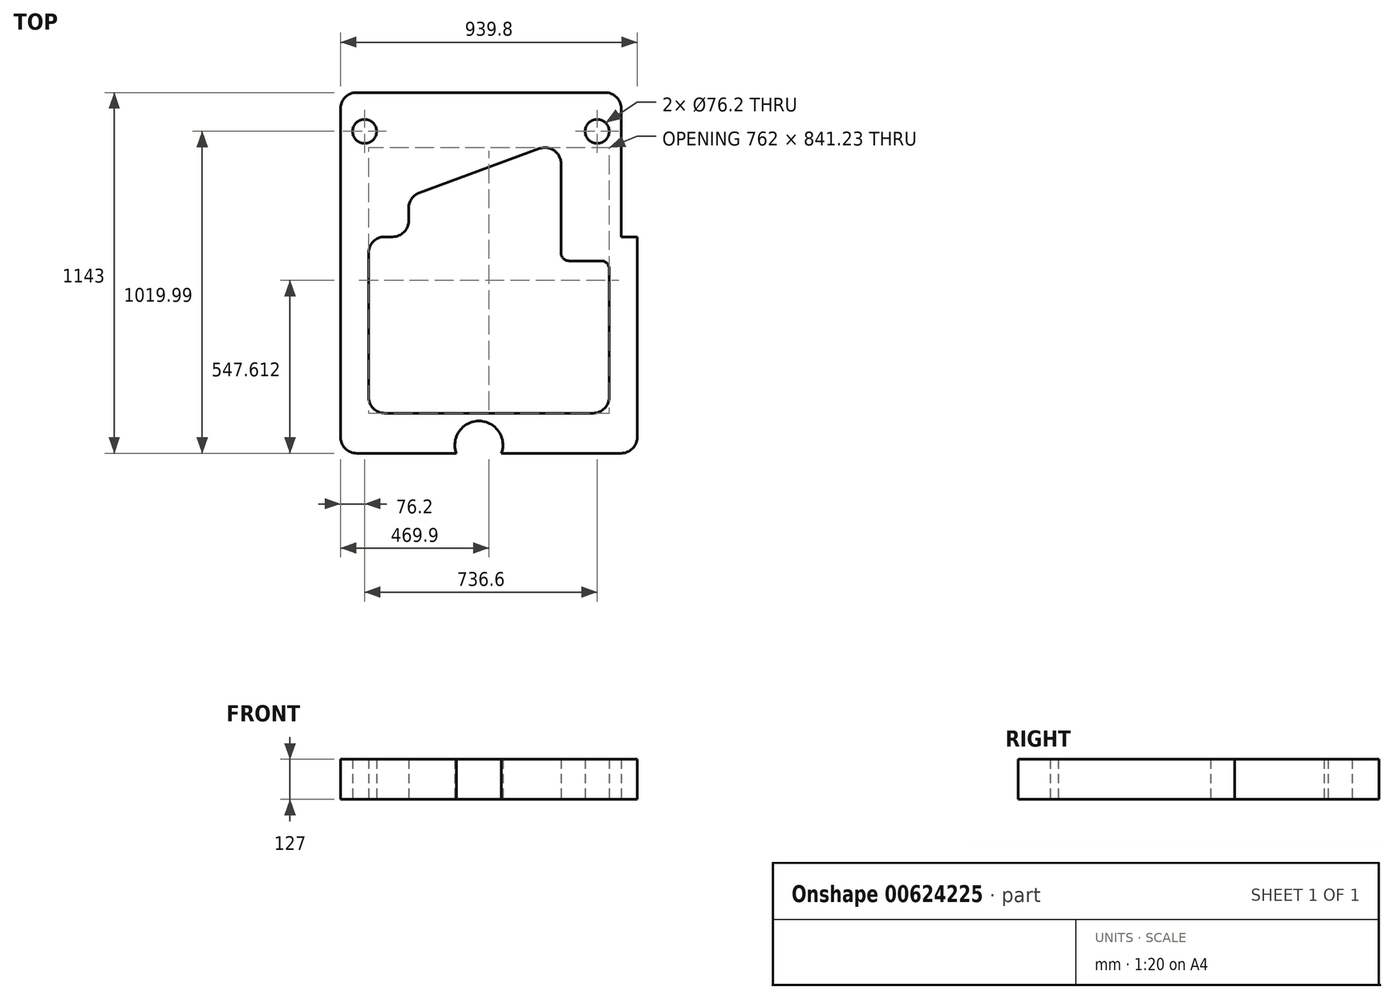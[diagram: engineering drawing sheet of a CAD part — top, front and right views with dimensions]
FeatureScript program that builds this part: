
annotation { "Feature Type Name" : "Feature", "Feature Type Description" : "" }
export const myFeature = defineFeature(function(context is Context, id is Id, definition is map)
    precondition{}
    {
        {
            var Q0;
            Q0=qCreatedBy(makeId("Top.planeOp"),FACE);
            var sketch = newSketch(context, id + "F0", { "sketchPlane" : qUnion([Q0])});
            skLineSegment(sketch, "E0.bottom", {"start": v(368.3, 571.5) * mm, "end": v(-419.1, 571.5) * mm});
            skLineSegment(sketch, "E0.top", {"start": v(419.1, -571.5) * mm, "end": v(-419.1, -571.5) * mm});
            skLineSegment(sketch, "E0.left", {"start": v(469.9, 114.3) * mm, "end": v(469.9, -520.7) * mm});
            skLineSegment(sketch, "E0.right", {"start": v(-469.9, 520.7) * mm, "end": v(-469.9, -520.7) * mm});
            skPoint(sketch, "E0.middle", {"position": v(0, 0) * mm});
            skLineSegment(sketch, "E1", {"start": v(-381, 63.5) * mm, "end": v(-381, -393.7) * mm});
            skLineSegment(sketch, "E2", {"start": v(-330.2, -444.5) * mm, "end": v(330.2, -444.5) * mm});
            skLineSegment(sketch, "E3", {"start": v(381, -393.7) * mm, "end": v(381, 12.7) * mm});
            skLineSegment(sketch, "E4", {"start": v(-330.2, 114.3) * mm, "end": v(-304.8, 114.3) * mm});
            skLineSegment(sketch, "E5", {"start": v(-254, 165.1) * mm, "end": v(-254, 205.88) * mm});
            skLineSegment(sketch, "E6", {"start": v(-220.76, 253.55) * mm, "end": v(160.24, 393.91) * mm});
            skLineSegment(sketch, "E7", {"start": v(228.6, 346.25) * mm, "end": v(228.6, 63.5) * mm});
            skLineSegment(sketch, "E8", {"start": v(254, 38.1) * mm, "end": v(355.6, 38.1) * mm});
            skLineSegment(sketch, "E9", {"start": v(419.1, 520.7) * mm, "end": v(419.1, 114.3) * mm});
            skLineSegment(sketch, "E10", {"start": v(419.1, 114.3) * mm, "end": v(508, 114.3) * mm});
            skPoint(sketch, "E11.orphan", {"position": v(469.9, 571.5) * mm});
            skPoint(sketch, "E12.visualSharp", {"position": v(-254, 114.3) * mm});
            skArc(sketch, "E12.filletArc", {"start": v(-304.8, 114.3) * mm, "mid": v(-268.88, 129.18) * mm, "end": v(-254, 165.1) * mm});
            skPoint(sketch, "E13.visualSharp", {"position": v(-381, 114.3) * mm});
            skArc(sketch, "E13.filletArc", {"start": v(-330.2, 114.3) * mm, "mid": v(-366.12, 99.42) * mm, "end": v(-381, 63.5) * mm});
            skPoint(sketch, "E14.visualSharp", {"position": v(-381, -444.5) * mm});
            skArc(sketch, "E14.filletArc", {"start": v(-381, -393.7) * mm, "mid": v(-366.12, -429.62) * mm, "end": v(-330.2, -444.5) * mm});
            skPoint(sketch, "E15.visualSharp", {"position": v(381, -444.5) * mm});
            skArc(sketch, "E15.filletArc", {"start": v(330.2, -444.5) * mm, "mid": v(366.12, -429.62) * mm, "end": v(381, -393.7) * mm});
            skPoint(sketch, "E16.visualSharp", {"position": v(-254, 241.3) * mm});
            skArc(sketch, "E16.filletArc", {"start": v(-220.76, 253.55) * mm, "mid": v(-244.87, 234.93) * mm, "end": v(-254, 205.88) * mm});
            skPoint(sketch, "E17.visualSharp", {"position": v(228.6, 419.1) * mm});
            skArc(sketch, "E17.filletArc", {"start": v(228.6, 346.25) * mm, "mid": v(206.86, 387.92) * mm, "end": v(160.24, 393.91) * mm});
            skPoint(sketch, "E18.visualSharp", {"position": v(228.6, 38.1) * mm});
            skArc(sketch, "E18.filletArc", {"start": v(228.6, 63.5) * mm, "mid": v(236.04, 45.54) * mm, "end": v(254, 38.1) * mm});
            skPoint(sketch, "E19.visualSharp", {"position": v(381, 38.1) * mm});
            skArc(sketch, "E19.filletArc", {"start": v(381, 12.7) * mm, "mid": v(373.56, 30.66) * mm, "end": v(355.6, 38.1) * mm});
            skPoint(sketch, "E20.visualSharp", {"position": v(-469.9, 571.5) * mm});
            skArc(sketch, "E20.filletArc", {"start": v(-419.1, 571.5) * mm, "mid": v(-455.02, 556.62) * mm, "end": v(-469.9, 520.7) * mm});
            skPoint(sketch, "E21.visualSharp", {"position": v(-469.9, -571.5) * mm});
            skArc(sketch, "E21.filletArc", {"start": v(-469.9, -520.7) * mm, "mid": v(-455.02, -556.62) * mm, "end": v(-419.1, -571.5) * mm});
            skPoint(sketch, "E22.visualSharp", {"position": v(469.9, -571.5) * mm});
            skArc(sketch, "E22.filletArc", {"start": v(419.1, -571.5) * mm, "mid": v(455.02, -556.62) * mm, "end": v(469.9, -520.7) * mm});
            skArc(sketch, "E23.filletArc", {"start": v(419.1, 520.7) * mm, "mid": v(404.22, 556.62) * mm, "end": v(368.3, 571.5) * mm});
            skLineSegment(sketch, "E24", {"start": v(-355.6, -508) * mm, "end": v(355.6, -508) * mm});
            skLineSegment(sketch, "E25", {"start": v(-381, -393.7) * mm, "end": v(-381, -482.6) * mm});
            skLineSegment(sketch, "E26", {"start": v(381, -393.7) * mm, "end": v(381, -482.6) * mm});
            skPoint(sketch, "E27.visualSharp", {"position": v(-381, -508) * mm});
            skArc(sketch, "E27.filletArc", {"start": v(-381, -482.6) * mm, "mid": v(-373.56, -500.56) * mm, "end": v(-355.6, -508) * mm});
            skPoint(sketch, "E28.visualSharp", {"position": v(381, -508) * mm});
            skArc(sketch, "E28.filletArc", {"start": v(355.6, -508) * mm, "mid": v(373.56, -500.56) * mm, "end": v(381, -482.6) * mm});
            skLineSegment(sketch, "E29", {"start": v(-31.69, -444.5) * mm, "end": v(-31.69, -624.57) * mm, "construction": true});
            skCircle(sketch, "E30", {"center": v(-31.69, -545.67) * mm, "radius": 76.2 * mm});
            skCircle(sketch, "E31", {"center": v(-31.69, -545.67) * mm, "radius": 38.1 * mm});
            skCircle(sketch, "E32", {"center": v(-393.7, 448.5) * mm, "radius": 76.2 * mm});
            skCircle(sketch, "E33", {"center": v(-393.7, 448.5) * mm, "radius": 38.1 * mm});
            skLineSegment(sketch, "E34", {"start": v(-393.7, 448.5) * mm, "end": v(350.76, 448.5) * mm, "construction": true});
            skCircle(sketch, "E35", {"center": v(342.9, 448.5) * mm, "radius": 76.2 * mm});
            skCircle(sketch, "E36", {"center": v(342.9, 448.5) * mm, "radius": 38.1 * mm});
            skSolve(sketch);
        }
        {
            var Q0;
            Q0=makeQuery(id+"F0.imprint","IMPRINT",FACE,{"disambiguationData":[TD([[makeQuery(id+"F0.imprint","IMPRINT",EDGE,{"derivedFrom":sQuery(id+"F0.wireOp",EDGE,"E2")}),-1.0]])]});
            extrude(context, id + "F1", {"entities" : qUnion([Q0]), "depth" : 50.8 * mm, "offsetDistance" : 25.4 * mm});
        }
        {
            var Q0;
            Q0=makeQuery(id+"F0.imprint","IMPRINT",FACE,{"disambiguationData":[TD([[makeQuery(id+"F0.imprint","IMPRINT",EDGE,{"derivedFrom":sQuery(id+"F0.wireOp",EDGE,"E0.bottom")}),1.0]])]});
            var Q1;
            Q1=makeQuery(id+"F0.imprint","IMPRINT",FACE,{"disambiguationData":[TD([[makeQuery(id+"F0.imprint","IMPRINT",EDGE,{"derivedFrom":sQuery(id+"F0.wireOp",EDGE,"E32")}),1.0]])]});
            var Q2;
            Q2=makeQuery(id+"F0.imprint","IMPRINT",FACE,{"disambiguationData":[TD([[makeQuery(id+"F0.imprint","IMPRINT",EDGE,{"derivedFrom":sQuery(id+"F0.wireOp",EDGE,"E35")}),1.0]])]});
            var Q3;
            {var subQ0=sQuery(id+"F0.wireOp",EDGE,"E30");var subQ1=sQuery(id+"F0.wireOp",EDGE,"E0.top");var subQ2=makeQuery(id+"F0.imprint","INTERSECT",VERTEX,{"disambiguationData":[OD(0.0)],"derivedFrom":[subQ1,subQ0]});Q3=makeQuery(id+"F0.imprint","IMPRINT",FACE,{"disambiguationData":[TD([[makeQuery(id+"F0.imprint","IMPRINT",EDGE,{"disambiguationData":[TD([[subQ2,-1.0]])],"derivedFrom":subQ1}),-1.0]])]});}
            var Q4;
            {var subQ0=sQuery(id+"F0.wireOp",EDGE,"E30");var subQ1=sQuery(id+"F0.wireOp",EDGE,"E24");var subQ2=makeQuery(id+"F0.imprint","INTERSECT",VERTEX,{"disambiguationData":[OD(0.0)],"derivedFrom":[subQ1,subQ0]});Q4=makeQuery(id+"F0.imprint","IMPRINT",FACE,{"disambiguationData":[TD([[makeQuery(id+"F0.imprint","IMPRINT",EDGE,{"disambiguationData":[TD([[subQ2,-1.0]])],"derivedFrom":subQ1}),1.0]])]});}
            var Q5;
            {var subQ0=sQuery(id+"F0.wireOp",EDGE,"E30");var subQ1=sQuery(id+"F0.wireOp",EDGE,"E0.top");var subQ2=makeQuery(id+"F0.imprint","INTERSECT",VERTEX,{"disambiguationData":[OD(1.0)],"derivedFrom":[subQ1,subQ0]});Q5=makeQuery(id+"F0.imprint","IMPRINT",FACE,{"disambiguationData":[TD([[makeQuery(id+"F0.imprint","IMPRINT",EDGE,{"disambiguationData":[TD([[subQ2,1.0]])],"derivedFrom":subQ1}),-1.0]])]});}
            var Q6;
            {var subQ0=sQuery(id+"F0.wireOp",EDGE,"E30");var subQ1=sQuery(id+"F0.wireOp",EDGE,"E0.top");var subQ2=makeQuery(id+"F0.imprint","INTERSECT",VERTEX,{"disambiguationData":[OD(0.0)],"derivedFrom":[subQ1,subQ0]});Q6=makeQuery(id+"F0.imprint","IMPRINT",FACE,{"disambiguationData":[TD([[makeQuery(id+"F0.imprint","IMPRINT",EDGE,{"disambiguationData":[TD([[subQ2,-1.0]])],"derivedFrom":subQ1}),1.0]])]});}
            extrude(context, id + "F2", {"entities" : qUnion([Q0, Q1, Q2, Q3, Q4, Q5, Q6]), "operationType" : NewBodyOperationType.ADD, "depth" : 127 * mm, "offsetDistance" : 25.4 * mm});
        }
    });
